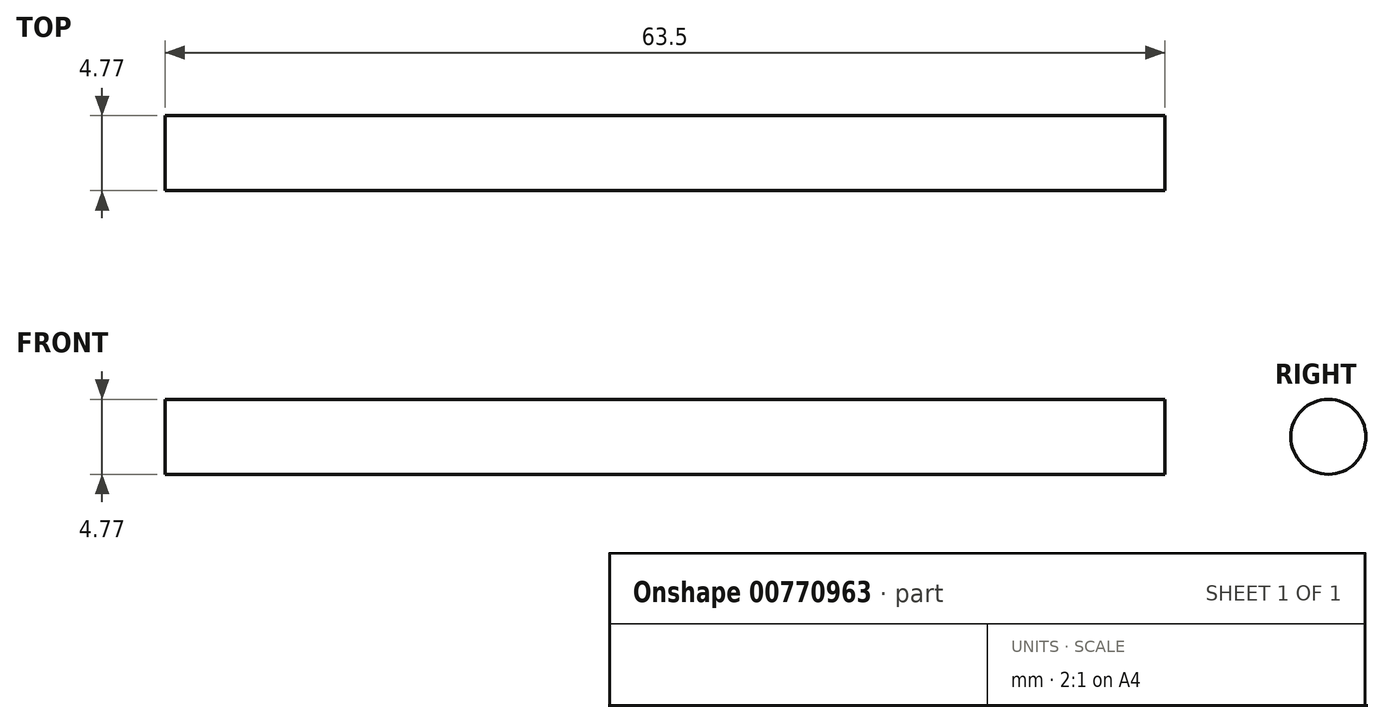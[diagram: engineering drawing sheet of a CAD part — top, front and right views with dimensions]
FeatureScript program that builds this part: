
annotation { "Feature Type Name" : "Feature", "Feature Type Description" : "" }
export const myFeature = defineFeature(function(context is Context, id is Id, definition is map)
    precondition{}
    {
        {
            var Q0;
            Q0=qCreatedBy(makeId("Right.planeOp"),FACE);
            var sketch = newSketch(context, id + "F0", { "sketchPlane" : qUnion([Q0])});
            skCircle(sketch, "E0", {"center": v(-13.53, 8.82) * mm, "radius": 2.38 * mm});
            skSolve(sketch);
        }
        {
            var Q0;
            Q0 = qSketchRegion(id + "F0", true);
            extrude(context, id + "F1", {"entities" : qUnion([Q0]), "depth" : 63.5 * mm, "offsetDistance" : 25.4 * mm});
        }
    });
